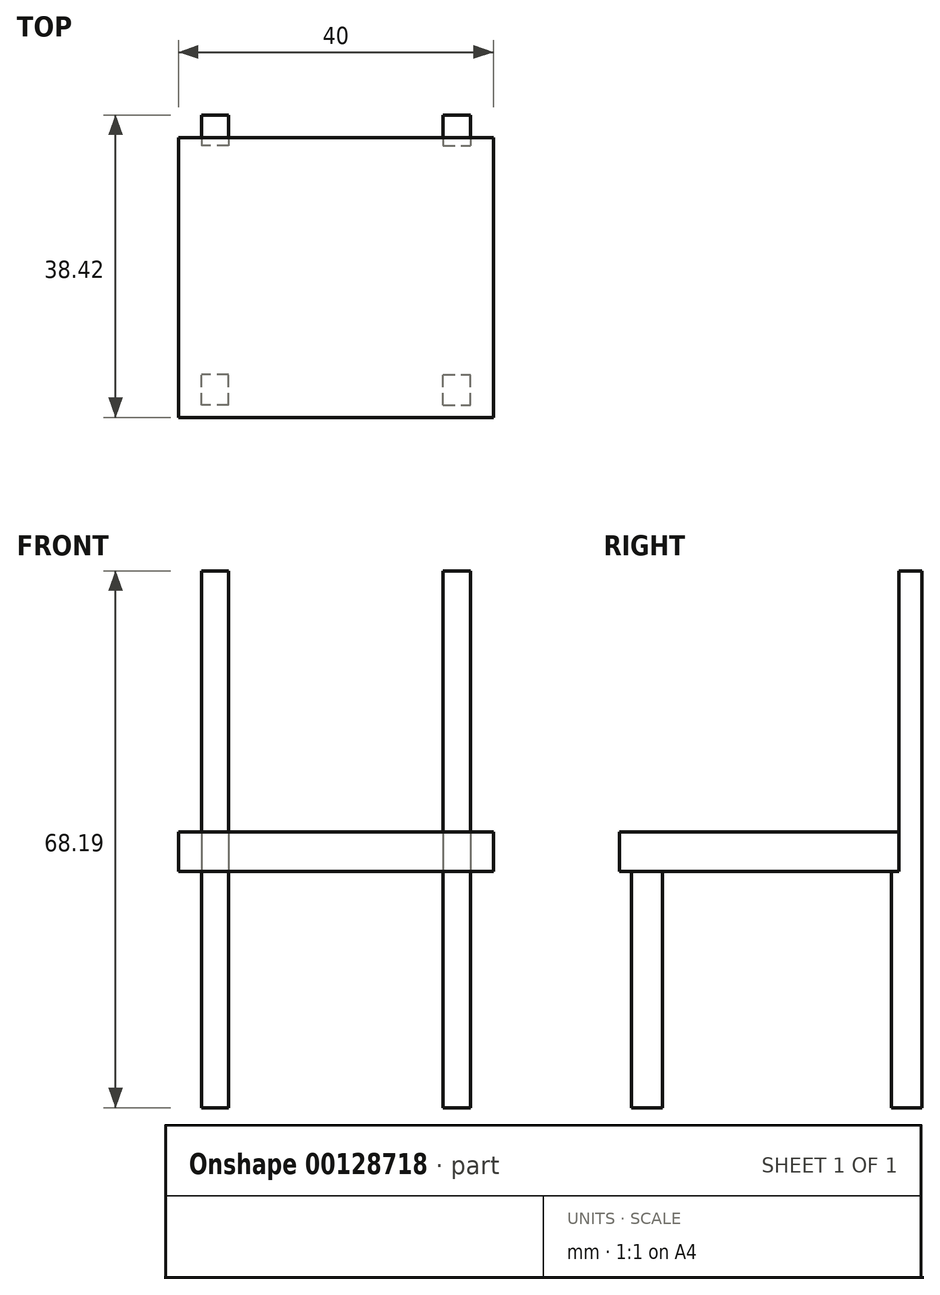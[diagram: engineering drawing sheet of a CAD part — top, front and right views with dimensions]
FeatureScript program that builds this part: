
annotation { "Feature Type Name" : "Feature", "Feature Type Description" : "" }
export const myFeature = defineFeature(function(context is Context, id is Id, definition is map)
    precondition{}
    {
        {
            var Q0;
            Q0=qCreatedBy(makeId("Top.planeOp"),FACE);
            var sketch = newSketch(context, id + "F0", { "sketchPlane" : qUnion([Q0])});
            skLineSegment(sketch, "E0.bottom", {"start": v(20, 20) * mm, "end": v(-20, 20) * mm});
            skLineSegment(sketch, "E0.top", {"start": v(20, -20) * mm, "end": v(-20, -20) * mm});
            skLineSegment(sketch, "E0.left", {"start": v(20, 20) * mm, "end": v(20, -20) * mm});
            skLineSegment(sketch, "E0.right", {"start": v(-20, 20) * mm, "end": v(-20, -20) * mm});
            skPoint(sketch, "E0.middle", {"position": v(0, 0) * mm});
            skLineSegment(sketch, "E1.bottom", {"start": v(-20, 20) * mm, "end": v(20, 20) * mm});
            skLineSegment(sketch, "E1.top", {"start": v(-20, 15.51) * mm, "end": v(20, 15.51) * mm});
            skLineSegment(sketch, "E1.left", {"start": v(-20, 20) * mm, "end": v(-20, 15.51) * mm});
            skLineSegment(sketch, "E1.right", {"start": v(20, 20) * mm, "end": v(20, 15.51) * mm});
            skLineSegment(sketch, "E2.bottom", {"start": v(13.6, 18.42) * mm, "end": v(17.07, 18.42) * mm});
            skLineSegment(sketch, "E2.top", {"start": v(13.6, 14.54) * mm, "end": v(17.07, 14.54) * mm});
            skLineSegment(sketch, "E2.left", {"start": v(13.6, 18.42) * mm, "end": v(13.6, 14.54) * mm});
            skLineSegment(sketch, "E2.right", {"start": v(17.07, 18.42) * mm, "end": v(17.07, 14.54) * mm});
            skLineSegment(sketch, "E3.MirrorCS", {"start": v(-13.6, 18.42) * mm, "end": v(-17.07, 18.42) * mm});
            skLineSegment(sketch, "E4.MirrorCS", {"start": v(-17.07, 18.42) * mm, "end": v(-17.07, 14.54) * mm});
            skLineSegment(sketch, "E5.MirrorCS", {"start": v(-13.6, 18.42) * mm, "end": v(-13.6, 14.54) * mm});
            skLineSegment(sketch, "E6.MirrorCS", {"start": v(-13.6, 14.54) * mm, "end": v(-17.07, 14.54) * mm});
            skLineSegment(sketch, "E7.MirrorCS", {"start": v(13.6, -14.54) * mm, "end": v(17.07, -14.54) * mm});
            skLineSegment(sketch, "E8.MirrorCS", {"start": v(17.07, -18.42) * mm, "end": v(17.07, -14.54) * mm});
            skLineSegment(sketch, "E9.MirrorCS", {"start": v(13.6, -18.42) * mm, "end": v(17.07, -18.42) * mm});
            skLineSegment(sketch, "E10.MirrorCS", {"start": v(13.6, -18.42) * mm, "end": v(13.6, -14.54) * mm});
            skLineSegment(sketch, "E11.MirrorCS", {"start": v(-13.6, -14.54) * mm, "end": v(-17.07, -14.54) * mm});
            skLineSegment(sketch, "E12.MirrorCS", {"start": v(-13.6, -18.42) * mm, "end": v(-13.6, -14.54) * mm});
            skLineSegment(sketch, "E13.MirrorCS", {"start": v(-13.6, -18.42) * mm, "end": v(-17.07, -18.42) * mm});
            skLineSegment(sketch, "E14.MirrorCS", {"start": v(-17.07, -18.42) * mm, "end": v(-17.07, -14.54) * mm});
            skSolve(sketch);
        }
        {
            var Q0;
            Q0=makeQuery(id+"F0.imprint","IMPRINT",FACE,{"disambiguationData":[TD([[makeQuery(id+"F0.imprint","IMPRINT",EDGE,{"derivedFrom":sQuery(id+"F0.wireOp",EDGE,"E7.MirrorCS")}),-1.0]])]});
            var Q1;
            Q1=makeQuery(id+"F0.imprint","IMPRINT",FACE,{"disambiguationData":[TD([[makeQuery(id+"F0.imprint","IMPRINT",EDGE,{"derivedFrom":sQuery(id+"F0.wireOp",EDGE,"E11.MirrorCS")}),1.0]])]});
            var Q2;
            {var subQ5=sQuery(id+"F0.wireOp",EDGE,"E2.bottom");Q2=makeQuery(id+"F0.imprint","IMPRINT",FACE,{"disambiguationData":[TD([[makeQuery(id+"F0.imprint","IMPRINT",EDGE,{"derivedFrom":subQ5}),-1.0]])]});}
            var Q3;
            {var subQ5=sQuery(id+"F0.wireOp",EDGE,"E2.top");Q3=makeQuery(id+"F0.imprint","IMPRINT",FACE,{"disambiguationData":[TD([[makeQuery(id+"F0.imprint","IMPRINT",EDGE,{"derivedFrom":subQ5}),1.0]])]});}
            var Q4;
            {var subQ5=sQuery(id+"F0.wireOp",EDGE,"E6.MirrorCS");Q4=makeQuery(id+"F0.imprint","IMPRINT",FACE,{"disambiguationData":[TD([[makeQuery(id+"F0.imprint","IMPRINT",EDGE,{"derivedFrom":subQ5}),-1.0]])]});}
            var Q5;
            {var subQ5=sQuery(id+"F0.wireOp",EDGE,"E3.MirrorCS");Q5=makeQuery(id+"F0.imprint","IMPRINT",FACE,{"disambiguationData":[TD([[makeQuery(id+"F0.imprint","IMPRINT",EDGE,{"derivedFrom":subQ5}),1.0]])]});}
            var Q6;
            Q6=makeQuery(id+"F0.imprint","IMPRINT",FACE,{"disambiguationData":[TD([[makeQuery(id+"F0.imprint","IMPRINT",EDGE,{"derivedFrom":sQuery(id+"F0.wireOp",EDGE,"E1.bottom")}),-1.0]])]});
            var Q7;
            Q7=makeQuery(id+"F0.imprint","IMPRINT",FACE,{"disambiguationData":[TD([[makeQuery(id+"F0.imprint","IMPRINT",EDGE,{"derivedFrom":sQuery(id+"F0.wireOp",EDGE,"E0.top")}),-1.0]])]});
            extrude(context, id + "F1", {"entities" : qUnion([Q0, Q1, Q2, Q3, Q4, Q5, Q6, Q7]), "depth" : 5 * mm});
        }
        {
            var Q0;
            Q0=makeQuery(id+"F0.imprint","IMPRINT",FACE,{"disambiguationData":[TD([[makeQuery(id+"F0.imprint","IMPRINT",EDGE,{"derivedFrom":sQuery(id+"F0.wireOp",EDGE,"E7.MirrorCS")}),-1.0]])]});
            var Q1;
            Q1=makeQuery(id+"F0.imprint","IMPRINT",FACE,{"disambiguationData":[TD([[makeQuery(id+"F0.imprint","IMPRINT",EDGE,{"derivedFrom":sQuery(id+"F0.wireOp",EDGE,"E11.MirrorCS")}),1.0]])]});
            var Q2;
            {var subQ5=sQuery(id+"F0.wireOp",EDGE,"E3.MirrorCS");Q2=makeQuery(id+"F0.imprint","IMPRINT",FACE,{"disambiguationData":[TD([[makeQuery(id+"F0.imprint","IMPRINT",EDGE,{"derivedFrom":subQ5}),1.0]])]});}
            var Q3;
            {var subQ5=sQuery(id+"F0.wireOp",EDGE,"E2.bottom");Q3=makeQuery(id+"F0.imprint","IMPRINT",FACE,{"disambiguationData":[TD([[makeQuery(id+"F0.imprint","IMPRINT",EDGE,{"derivedFrom":subQ5}),-1.0]])]});}
            var Q4;
            {var subQ5=sQuery(id+"F0.wireOp",EDGE,"E2.top");Q4=makeQuery(id+"F0.imprint","IMPRINT",FACE,{"disambiguationData":[TD([[makeQuery(id+"F0.imprint","IMPRINT",EDGE,{"derivedFrom":subQ5}),1.0]])]});}
            var Q5;
            {var subQ5=sQuery(id+"F0.wireOp",EDGE,"E6.MirrorCS");Q5=makeQuery(id+"F0.imprint","IMPRINT",FACE,{"disambiguationData":[TD([[makeQuery(id+"F0.imprint","IMPRINT",EDGE,{"derivedFrom":subQ5}),-1.0]])]});}
            extrude(context, id + "F2", {"entities" : qUnion([Q0, Q1, Q2, Q3, Q4, Q5]), "operationType" : NewBodyOperationType.ADD, "oppositeDirection" : true, "depth" : 30 * mm});
        }
        {
            var Q0;
            Q0=makeQuery(id+"F0.imprint","IMPRINT",FACE,{"disambiguationData":[TD([[makeQuery(id+"F0.imprint","IMPRINT",EDGE,{"derivedFrom":sQuery(id+"F0.wireOp",EDGE,"E1.bottom")}),-1.0]])]});
            var Q1;
            {var subQ5=sQuery(id+"F0.wireOp",EDGE,"E3.MirrorCS");Q1=makeQuery(id+"F0.imprint","IMPRINT",FACE,{"disambiguationData":[TD([[makeQuery(id+"F0.imprint","IMPRINT",EDGE,{"derivedFrom":subQ5}),1.0]])]});}
            var Q2;
            {var subQ5=sQuery(id+"F0.wireOp",EDGE,"E2.bottom");Q2=makeQuery(id+"F0.imprint","IMPRINT",FACE,{"disambiguationData":[TD([[makeQuery(id+"F0.imprint","IMPRINT",EDGE,{"derivedFrom":subQ5}),-1.0]])]});}
            extrude(context, id + "F3", {"entities" : qUnion([Q0, Q1, Q2]), "operationType" : NewBodyOperationType.ADD, "depth" : 38.2 * mm});
        }
        {
            var Q0;
            Q0=makeQuery(id+"F3.opExtrude","SWEPT_FACE",FACE,{"disambiguationData":[OSD([sQuery(id+"F0.wireOp",EDGE,"E1.top")])]});
            var sketch = newSketch(context, id + "F4", { "sketchPlane" : qUnion([Q0])});
            skCircle(sketch, "E15", {"center": v(0, 23.22) * mm, "radius": 9.3 * mm});
            skSolve(sketch);
        }
        {
            var Q0;
            Q0 = qSketchRegion(id + "F4", true);
            extrude(context, id + "F5", {"entities" : qUnion([Q0]), "operationType" : NewBodyOperationType.REMOVE, "endBound" : BoundingType.THROUGH_ALL, "oppositeDirection" : true, "depth" : 25 * mm});
        }
    });
